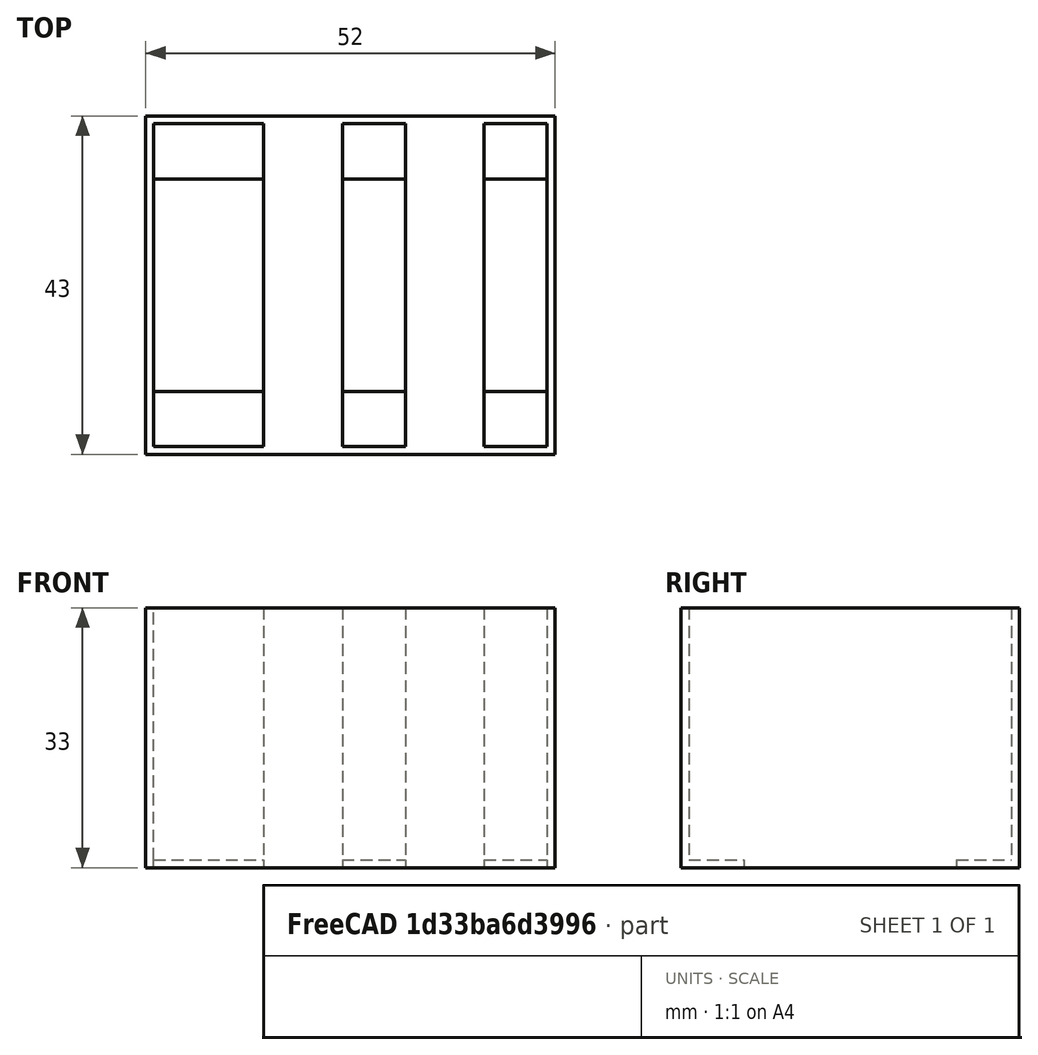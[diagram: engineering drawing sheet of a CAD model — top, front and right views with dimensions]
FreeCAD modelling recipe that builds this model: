
FCSTD DOCUMENT  (FreeCAD 0.18R4 (GitTag))
Label: lost_realms
License: All rights reserved
LicenseURL: http://en.wikipedia.org/wiki/All_rights_reserved
objects: Part::Box×8, Part::Cut×2, Part::MultiFuse×2
note: 12 computed .brp shape members not serialized (recipe doc carries the construction recipe); baked Part::Feature solids carry a one-line shape summary decoded from their .brp

FEATURE [Part::Box] Box  label="Cube"
  AttacherType = Attacher::AttachEngine3D
  Height = 33
  Length = 202
  Width = 43
FEATURE [Part::Box] Box001  label="Cube001"
  AttacherType = Attacher::AttachEngine3D
  Height = 33
  Length = 200
  Placement = pos=(1,1,0) rot=(0,0,1;0rad)
  Width = 41
FEATURE [Part::Cut] Cut
  Base = -> Box
  Tool = -> Box001
FEATURE [Part::Box] Box002  label="Cube002"
  AttacherType = Attacher::AttachEngine3D
  Height = 1
  Length = 202
  Width = 8
FEATURE [Part::Box] Box003  label="Cube003"
  AttacherType = Attacher::AttachEngine3D
  Height = 1
  Length = 202
  Placement = pos=(0,35,0) rot=(0,0,1;0rad)
  Width = 8
FEATURE [Part::MultiFuse] Fusion
  Shapes = -> [Cut,Box002,Box003]
FEATURE [Part::Box] Box004  label="Cube004"
  AttacherType = Attacher::AttachEngine3D
  Height = 33
  Length = 10
  Placement = pos=(15,0,0) rot=(0,0,1;0rad)
  Width = 43
FEATURE [Part::Box] Box005  label="Cube005"
  AttacherType = Attacher::AttachEngine3D
  Height = 33
  Length = 10
  Placement = pos=(33,0,0) rot=(0,0,1;0rad)
  Width = 43
FEATURE [Part::Box] Box006  label="Cube006"
  AttacherType = Attacher::AttachEngine3D
  Height = 33
  Length = 10
  Placement = pos=(51,0,0) rot=(0,0,1;0rad)
  Width = 43
FEATURE [Part::Box] Box007  label="Cube007"
  AttacherType = Attacher::AttachEngine3D
  Height = 33
  Length = 150
  Placement = pos=(52,0,0) rot=(0,0,1;0rad)
  Width = 43
FEATURE [Part::MultiFuse] Fusion001
  Shapes = -> [Fusion,Box005,Box004,Box006]
FEATURE [Part::Cut] Cut001
  Base = -> Fusion001
  Tool = -> Box007
